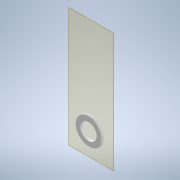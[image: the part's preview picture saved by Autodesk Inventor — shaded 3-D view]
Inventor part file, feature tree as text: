
AUTODESK INVENTOR PART (.ipt)
format: ipt  version: 2021 (Build 250183000, 183)  size: 130,560 bytes
history: native  units: mm
features: other x5, extrude x1, fillet x1, sketch x1, reference x1
ambient origin geometry x8: Origin, YZ Plane, XZ Plane, XY Plane, X Axis, Y Axis, Z Axis, Center Point
bodies: Body1 (feature_tree)
feature tree (9):
  other  "Bryła1"
  other  "Płaszczyzna konstrukcyjna1"
  extrude  "Wyciągnięcie proste1"  Depth=6.0mm
  fillet  "Zaokrąglenie1"  Radius=20.0mm
  sketch  "Szkic1"
  reference  "Odniesienie1"
  parser-record x1  (decoder bookkeeping rows leaked as tree rows — omitted from the tree; the rows remain in map.json)
  other  "zespoluchwyt.iam"
  other  "uchwyt1:1"
note: 1 file-system path scrubbed to <path> (originals preserved in map.json)
